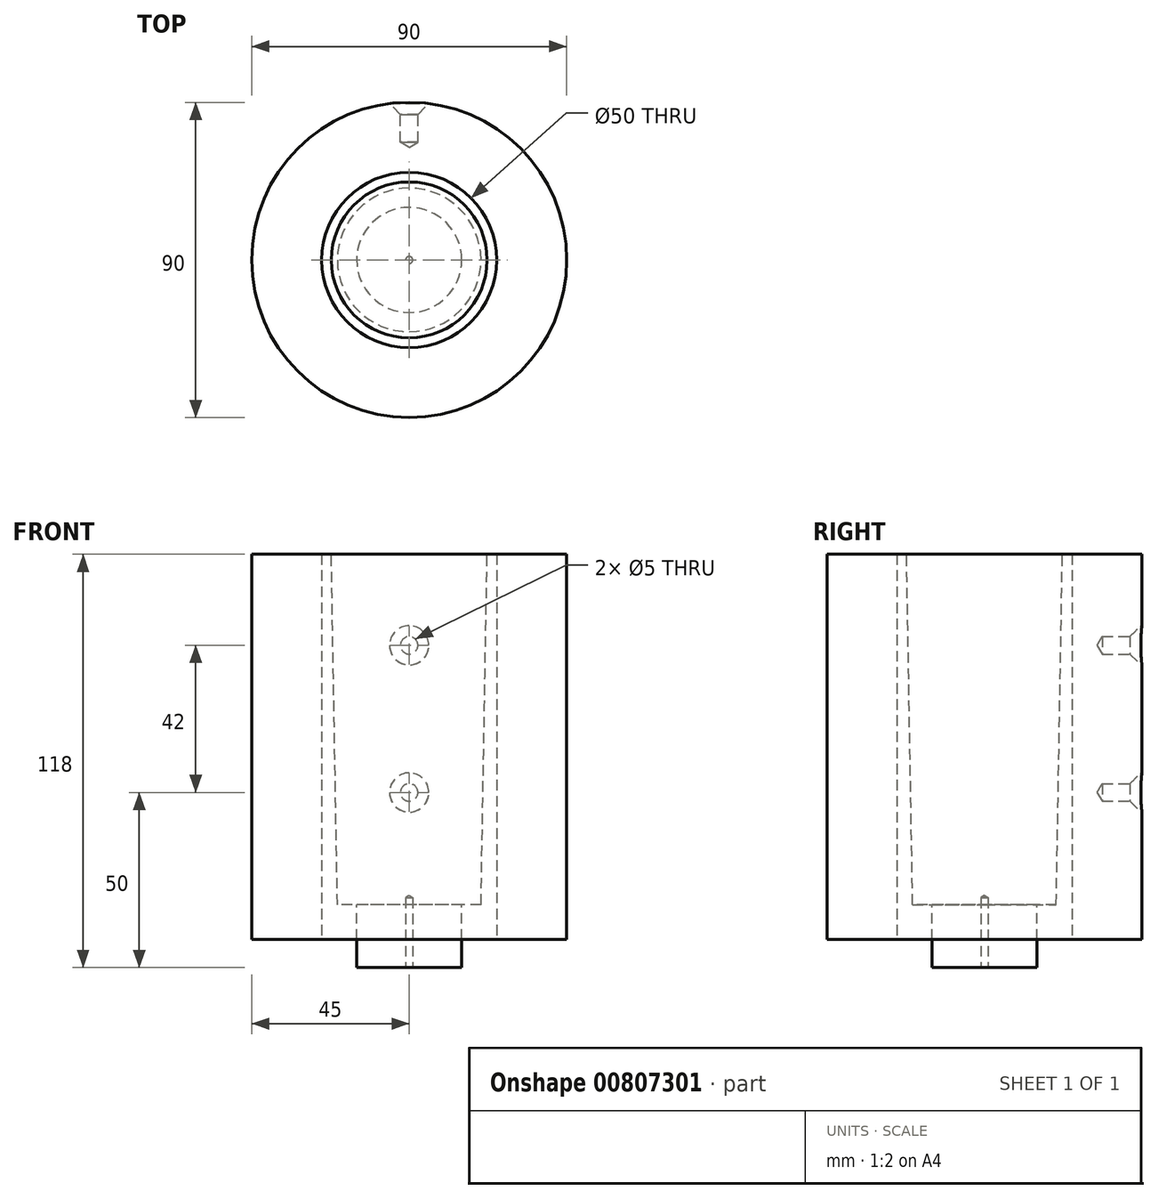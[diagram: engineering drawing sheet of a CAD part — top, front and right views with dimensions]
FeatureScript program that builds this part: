
annotation { "Feature Type Name" : "Feature", "Feature Type Description" : "" }
export const myFeature = defineFeature(function(context is Context, id is Id, definition is map)
    precondition{}
    {
        {
            var Q0;
            Q0=qCreatedBy(makeId("Front.planeOp"),FACE);
            var sketch = newSketch(context, id + "F0", { "sketchPlane" : qUnion([Q0])});
            skLineSegment(sketch, "E0", {"start": v(15, 0) * mm, "end": v(15, -18) * mm});
            skLineSegment(sketch, "E1", {"start": v(15, -18) * mm, "end": v(0, -18) * mm});
            skLineSegment(sketch, "E2", {"start": v(15, 0) * mm, "end": v(20.5, 0) * mm});
            skLineSegment(sketch, "E3", {"start": v(0, 200) * mm, "end": v(24, 200) * mm});
            skLineSegment(sketch, "E4", {"start": v(24, 200) * mm, "end": v(20.5, 0) * mm});
            skLineSegment(sketch, "E5", {"start": v(0, 200) * mm, "end": v(0, -18) * mm});
            skPoint(sketch, "E6", {"position": v(0, -18) * mm});
            skPoint(sketch, "E7", {"position": v(0, 0) * mm});
            skPoint(sketch, "E8", {"position": v(0, -10) * mm});
            skSolve(sketch);
        }
        {
            var Q0;
            Q0=makeQuery(id+"F0.imprint","IMPRINT",FACE,{"disambiguationData":[TD([[makeQuery(id+"F0.imprint","IMPRINT",EDGE,{"derivedFrom":sQuery(id+"F0.wireOp",EDGE,"E0")}),-1.0]])]});
            var Q1;
            Q1=sQuery(id+"F0.wireOp",EDGE,"E5");
            revolve(context, id + "F1", {"entities" : qUnion([Q0]), "axis" : qUnion([Q1]), "revolveType" : RevolveType.FULL});
        }
        {
            var Q0;
            Q0=qCreatedBy(makeId("Top.planeOp"),FACE);
            cPlane(context, id + "F2", {"entities" : qUnion([Q0]), "cplaneType" : CPlaneType.OFFSET, "offset" : 47 * mm, "oppositeDirection" : true, "width" : 150 * mm, "height" : 150 * mm});
        }
        {
            var Q0;
            Q0=qCreatedBy(id+"F2.planeOp",FACE);
            cPlane(context, id + "F3", {"entities" : qUnion([Q0]), "cplaneType" : CPlaneType.OFFSET, "offset" : 517 * mm, "width" : 150 * mm, "height" : 150 * mm});
        }
        {
            var Q0;
            Q0=qCreatedBy(id+"F2.planeOp",FACE);
            var sketch = newSketch(context, id + "F4", { "sketchPlane" : qUnion([Q0])});
            skPoint(sketch, "E9", {"position": v(0, 0) * mm});
            skSolve(sketch);
        }
        {
            var Q0;
            Q0=qCreatedBy(id+"F3.planeOp",FACE);
            var sketch = newSketch(context, id + "F5", { "sketchPlane" : qUnion([Q0])});
            skPoint(sketch, "E10", {"position": v(0, 0) * mm});
            skSolve(sketch);
        }
        {
            var Q0;
            Q0=sQuery(id+"F4.wireOp",VERTEX,"E9");
            var Q1;
            Q1=makeQuery(id+"F1.opRevolve","SWEPT_BODY",BODY,{"disambiguationData":[OSD([sQuery(id+"F0.wireOp",EDGE,"E0"),sQuery(id+"F0.wireOp",EDGE,"E1"),sQuery(id+"F0.wireOp",EDGE,"E2"),sQuery(id+"F0.wireOp",EDGE,"E3"),sQuery(id+"F0.wireOp",EDGE,"E4"),sQuery(id+"F0.wireOp",EDGE,"E5")])]});
            hole(context, id + "F6", {"style" : HoleStyle.C_SINK, "endStyle" : HoleEndStyle.BLIND, "oppositeDirection" : true, "holeDiameter" : 2 * mm, "cSinkDiameter" : 2 * mm, "cSinkAngle" : 90 * degree, "holeDepth" : 20 * mm, "isTappedThrough" : true, "tappedDepth" : 12 * mm, "tapClearance" : 3, "locations" : qUnion([Q0]), "scope" : qUnion([Q1])});
        }
        {
            var Q0;
            Q0=qCreatedBy(makeId("Front.planeOp"),FACE);
            var sketch = newSketch(context, id + "F7", { "sketchPlane" : qUnion([Q0])});
            skLineSegment(sketch, "E11", {"start": v(-25, -10) * mm, "end": v(-45, -10) * mm});
            skLineSegment(sketch, "E12", {"start": v(-45, -10) * mm, "end": v(-45, 200) * mm});
            skLineSegment(sketch, "E13", {"start": v(-45, 200) * mm, "end": v(-25, 200) * mm});
            skLineSegment(sketch, "E14", {"start": v(-25, 200) * mm, "end": v(-25, -10) * mm});
            skLineSegment(sketch, "E15", {"start": v(0, -77.16) * mm, "end": v(0, 437.55) * mm});
            skPoint(sketch, "E16", {"position": v(0, 0) * mm});
            skPoint(sketch, "E17", {"position": v(0, -10) * mm});
            skPoint(sketch, "E18", {"position": v(-25, -10) * mm});
            skSolve(sketch);
        }
        {
            var Q0;
            Q0=makeQuery(id+"F7.imprint","IMPRINT",FACE,{"disambiguationData":[TD([[makeQuery(id+"F7.imprint","IMPRINT",EDGE,{"derivedFrom":sQuery(id+"F7.wireOp",EDGE,"E11")}),-1.0]])]});
            var Q1;
            Q1=sQuery(id+"F7.wireOp",EDGE,"E15");
            revolve(context, id + "F8", {"entities" : qUnion([Q0]), "axis" : qUnion([Q1]), "revolveType" : RevolveType.FULL});
        }
        {
            var Q0;
            Q0=qCreatedBy(makeId("Right.planeOp"),FACE);
            var sketch = newSketch(context, id + "F9", { "sketchPlane" : qUnion([Q0])});
            skLineSegment(sketch, "E19", {"start": v(0, 0) * mm, "end": v(50, 0) * mm});
            skSolve(sketch);
        }
        {
            var Q0;
            Q0=sQuery(id+"F9.wireOp",VERTEX,"E19.end");
            var Q1;
            Q1=sQuery(id+"F9.wireOp",EDGE,"E19");
            cPlane(context, id + "F10", {"entities" : qUnion([Q0, Q1]), "cplaneType" : CPlaneType.LINE_POINT, "offset" : 25 * mm, "width" : 150 * mm, "height" : 150 * mm});
        }
        {
            var Q0;
            Q0=qCreatedBy(id+"F10.planeOp",FACE);
            var sketch = newSketch(context, id + "F11", { "sketchPlane" : qUnion([Q0])});
            skLineSegment(sketch, "E20", {"start": v(0, -10) * mm, "end": v(0, 158) * mm});
            skPoint(sketch, "E21", {"position": v(0, 32) * mm});
            skPoint(sketch, "E22", {"position": v(0, 74) * mm});
            skPoint(sketch, "E23", {"position": v(0, 116) * mm});
            skPoint(sketch, "E24", {"position": v(0, 158) * mm});
            skSolve(sketch);
        }
        {
            var Q0;
            Q0=sQuery(id+"F11.wireOp",VERTEX,"E21");
            var Q1;
            Q1=sQuery(id+"F11.wireOp",VERTEX,"E22");
            var Q2;
            Q2=sQuery(id+"F11.wireOp",VERTEX,"E23");
            var Q3;
            Q3=sQuery(id+"F11.wireOp",VERTEX,"E24");
            var Q4;
            Q4=sQuery(id+"F11.wireOp",VERTEX,"40b30d50-acc6-4a72-9d00-9dda39e924d6");
            var Q5;
            Q5=sQuery(id+"F11.wireOp",VERTEX,"77082208-eed3-454b-b085-99042ab40a85");
            var Q6;
            Q6=sQuery(id+"F11.wireOp",VERTEX,"609133c0-56c0-4d15-a277-36ce9413017b");
            var Q7;
            Q7=sQuery(id+"F11.wireOp",VERTEX,"6793db04-1c17-4af6-bba2-8a63467633aa");
            var Q8;
            Q8=makeQuery(id+"F8.opRevolve","SWEPT_BODY",BODY,{"disambiguationData":[OSD([sQuery(id+"F7.wireOp",EDGE,"E11"),sQuery(id+"F7.wireOp",EDGE,"E12"),sQuery(id+"F7.wireOp",EDGE,"E13"),sQuery(id+"F7.wireOp",EDGE,"E14")])]});
            hole(context, id + "F12", {"style" : HoleStyle.C_SINK, "endStyle" : HoleEndStyle.BLIND, "holeDiameter" : 5 * mm, "cSinkDiameter" : 11.2 * mm, "cSinkAngle" : 90 * degree, "holeDepth" : 11 * mm, "isTappedThrough" : true, "tappedDepth" : 12 * mm, "tapClearance" : 3, "locations" : qUnion([Q0, Q1, Q2, Q3, Q4, Q5, Q6, Q7]), "scope" : qUnion([Q8])});
        }
        {
            var Q0;
            Q0=sQuery(id+"F5.wireOp",VERTEX,"E10");
            var Q1;
            Q1=makeQuery(id+"F1.opRevolve","SWEPT_BODY",BODY,{"disambiguationData":[OSD([sQuery(id+"F0.wireOp",EDGE,"E0"),sQuery(id+"F0.wireOp",EDGE,"E1"),sQuery(id+"F0.wireOp",EDGE,"E2"),sQuery(id+"F0.wireOp",EDGE,"E3"),sQuery(id+"F0.wireOp",EDGE,"E4"),sQuery(id+"F0.wireOp",EDGE,"E5")])]});
            hole(context, id + "F13", {"style" : HoleStyle.C_SINK, "endStyle" : HoleEndStyle.BLIND, "holeDiameter" : 2 * mm, "cSinkDiameter" : 5 * mm, "cSinkAngle" : 90 * degree, "holeDepth" : 20 * mm, "isTappedThrough" : true, "tappedDepth" : 12 * mm, "tapClearance" : 3, "locations" : qUnion([Q0]), "scope" : qUnion([Q1])});
        }
        {
            var Q0;
            Q0=qCreatedBy(makeId("Top.planeOp"),FACE);
            cPlane(context, id + "F14", {"entities" : qUnion([Q0]), "cplaneType" : CPlaneType.OFFSET, "offset" : 100 * mm, "width" : 150 * mm, "height" : 150 * mm});
        }
        {
            var Q0;
            Q0=qCreatedBy(id+"F14.planeOp",FACE);
            var sketch = newSketch(context, id + "F15", { "sketchPlane" : qUnion([Q0])});
            skLineSegment(sketch, "E25.bottom", {"start": v(-62.54, -66.9) * mm, "end": v(62.54, -66.9) * mm});
            skLineSegment(sketch, "E25.top", {"start": v(-62.54, 66.9) * mm, "end": v(62.54, 66.9) * mm});
            skLineSegment(sketch, "E25.left", {"start": v(-62.54, -66.9) * mm, "end": v(-62.54, 66.9) * mm});
            skLineSegment(sketch, "E25.right", {"start": v(62.54, -66.9) * mm, "end": v(62.54, 66.9) * mm});
            skPoint(sketch, "E25.middle", {"position": v(0, 0) * mm});
            skSolve(sketch);
        }
        {
            var Q0;
            Q0=makeQuery(id+"F15.imprint","IMPRINT",FACE,{"disambiguationData":[TD([[makeQuery(id+"F15.imprint","IMPRINT",EDGE,{"derivedFrom":sQuery(id+"F15.wireOp",EDGE,"E25.bottom")}),1.0]])]});
            extrude(context, id + "F16", {"entities" : qUnion([Q0]), "operationType" : NewBodyOperationType.REMOVE, "depth" : 100 * mm, "offsetDistance" : 25 * mm});
        }
    });
